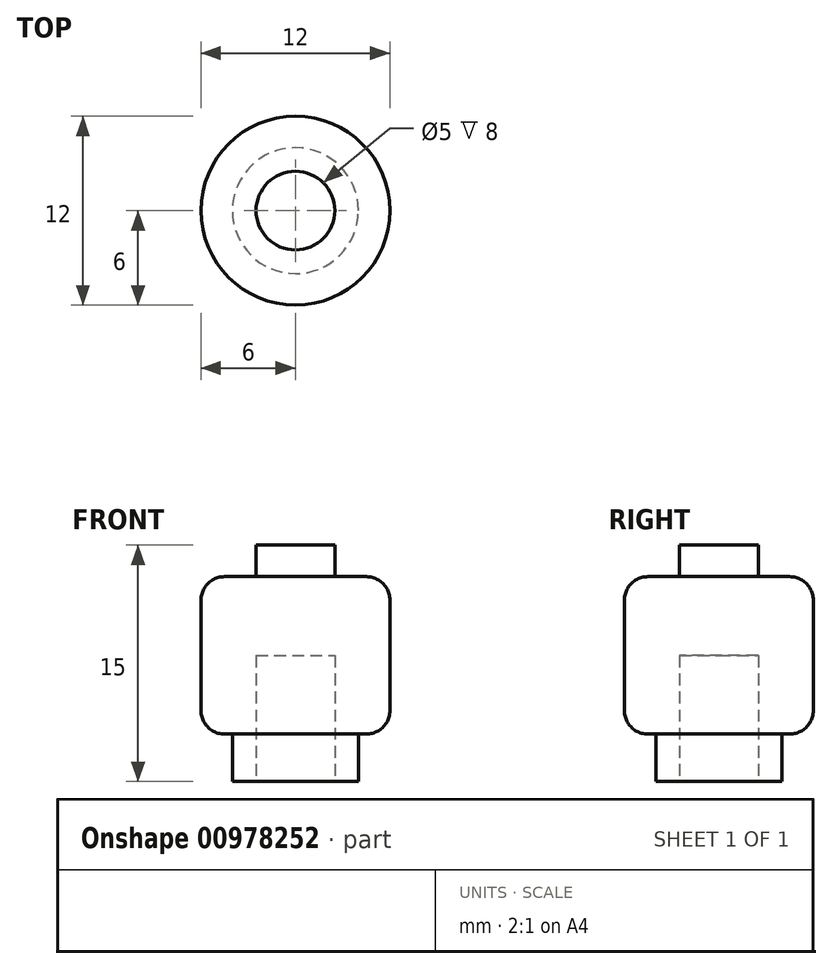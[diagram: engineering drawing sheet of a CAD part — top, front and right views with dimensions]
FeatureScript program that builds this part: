
annotation { "Feature Type Name" : "Feature", "Feature Type Description" : "" }
export const myFeature = defineFeature(function(context is Context, id is Id, definition is map)
    precondition{}
    {
        {
            var Q0;
            Q0=qCreatedBy(makeId("Top.planeOp"),FACE);
            var sketch = newSketch(context, id + "F0", { "sketchPlane" : qUnion([Q0])});
            skCircle(sketch, "E0", {"center": v(0, 0) * mm, "radius": 4 * mm});
            skSolve(sketch);
        }
        {
            var Q0;
            Q0=qSketchRegion(id+"F0",true);
            extrude(context, id + "F1", {"entities" : qUnion([Q0]), "depth" : 3 * mm, "offsetDistance" : 25.4 * mm});
        }
        {
            var Q0;
            Q0=makeQuery(id+"F1.opExtrude","CAP_FACE",FACE,{"disambiguationData":[OSD([sQuery(id+"F0.wireOp",EDGE,"E0")])],"isStart":false});
            var sketch = newSketch(context, id + "F2", { "sketchPlane" : qUnion([Q0])});
            skCircle(sketch, "E1", {"center": v(0, 0) * mm, "radius": 6 * mm});
            skSolve(sketch);
        }
        {
            var Q0;
            Q0=qSketchRegion(id+"F2",true);
            extrude(context, id + "F3", {"entities" : qUnion([Q0]), "operationType" : NewBodyOperationType.ADD, "depth" : 10 * mm, "offsetDistance" : 25.4 * mm});
        }
        {
            var Q0;
            Q0=makeQuery(id+"F3.opExtrude","CAP_FACE",FACE,{"disambiguationData":[OSD([sQuery(id+"F2.wireOp",EDGE,"E1")])],"isStart":false});
            var sketch = newSketch(context, id + "F4", { "sketchPlane" : qUnion([Q0])});
            skCircle(sketch, "E2", {"center": v(0, 0) * mm, "radius": 2.5 * mm});
            skSolve(sketch);
        }
        {
            var Q0;
            Q0=qSketchRegion(id+"F4",true);
            extrude(context, id + "F5", {"entities" : qUnion([Q0]), "operationType" : NewBodyOperationType.ADD, "depth" : 2 * mm, "offsetDistance" : 25.4 * mm});
        }
        {
            var Q0;
            Q0=makeQuery(id+"F3.opExtrude","CAP_EDGE",EDGE,{"disambiguationData":[OSD([sQuery(id+"F2.wireOp",EDGE,"E1")])],"isStart":false});
            var Q1;
            Q1=makeQuery(id+"F3.opExtrude","CAP_EDGE",EDGE,{"disambiguationData":[OSD([sQuery(id+"F2.wireOp",EDGE,"E1")])],"isStart":true});
            fillet(context, id + "F6", {"entities" : qUnion([Q0, Q1]), "radius" : 1.5 * mm, "tangentPropagation" : true, "allowEdgeOverflow" : false});
        }
        {
            var Q0;
            Q0=makeQuery(id+"F1.opExtrude","CAP_FACE",FACE,{"disambiguationData":[OSD([sQuery(id+"F0.wireOp",EDGE,"E0")])],"isStart":true});
            var sketch = newSketch(context, id + "F7", { "sketchPlane" : qUnion([Q0])});
            skCircle(sketch, "E3", {"center": v(0, 0) * mm, "radius": 2.5 * mm});
            skSolve(sketch);
        }
        {
            var Q0;
            Q0=qSketchRegion(id+"F7",true);
            extrude(context, id + "F8", {"entities" : qUnion([Q0]), "operationType" : NewBodyOperationType.REMOVE, "oppositeDirection" : true, "depth" : 8 * mm, "offsetDistance" : 25.4 * mm});
        }
    });
